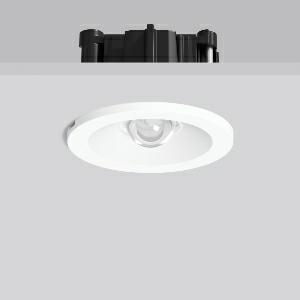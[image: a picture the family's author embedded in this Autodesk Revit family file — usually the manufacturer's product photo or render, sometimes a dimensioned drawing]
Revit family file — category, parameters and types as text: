
# Revit family: turia_l_672413_002_04_6de2
name_source: partatom
category: Lighting Fixtures
units: mm (PartAtom-declared; Revit-internal decimal feet)

## family parameters
Cut with Voids When Loaded = No
Host = Face
Light Source = No
Part Type = Normal
Room Calculation Point = No
Round Connector Dimension = Use Diameter
Shared = No

## types (1)
- TURIA L (1 x LED Modul 765, 270 lm, 6500)
    Apparent Load = 5 VA
    CIE Flux Codes = 16 58 99 100 100
    Color Rendering = 70
    Color Temperature = 6500
    Default Elevation = 1800 mm
    Description = Series: TURIA L
Round emergency luminaire for escape route lighting. Housing: die-cast aluminium. Bezel ring: plastic. With plastic lenses for area lighting. Self-contained system with automatic self-test and feedback to the RZB monitoring system MULTIDIGIT. With enclosed separate ceiling mounting ring also suitable for ceiling cut-outs of Ø 68 mm. 
Colour: white
Diameter: 62 mm
Height: 3 mm
Cut-out diameter: 54-68 mm
Recess height: 76-162 mm
Luminaire: recess height: 42 mm
Weight: 550 g
Operating mode: non-maintained power mode
Duration time: 8 h
Lamp: LED
Socket: without socket
Colour temperature: 6500K
Colour rendering index (CRI): 70
System power: 5.2 W
Rated luminous flux: 270 lm
Luminous flux, emergency: 130 lm
System power, emergency: -
Control gear: Regulated power supply
Protection class: II
Type of protection: IP 20
    Height = 0 mm  [stored 0 ft]
    Lamp = 1 x LED Modul 765
    Lamp Light Flux = 270 lm
    Lamp count = 1
    Length = 62 mm  [stored 0.203412 ft]
    Lifetime = 50000 h
    Luminous efficacy = 52 lm/W
    Manufacturer = RZB
    ModVariant = No
    Model = 672413.002.04
    Mounting Place = Ceiling
    Mounting Type = Recessed
    Number of Poles = 1
    OnlyDefault = Yes
    Power Factor = 1
    Product Name = TURIA L
    Product group = Recessed ceiling luminaires
    ProductGroupID = 405
    Protection Class = Protection class II
    Protection Degree = IP 20
    RLX_Detail_Level = 1
    RLX_Emergency_Light_Flux = 130 lm
    RLX_Emergency_Type = 3
    RLX_Emergency_Type_DB = Yes
    RlxData = <blob elided: 35689 chars, md5=a92c01f5>
    Socket = socket
    Standby Power = 0 W
    System Light Flux = 270 lm
    System Power = 5 W
    Type Comments = Product without accessories
    Type Image = 672412.002.jpg
    URL = http://relux.com
    VarID = ---
    Voltage = 230 V
    Voltage Range = 220-240 V
    Weight = 0.00 kg
    Width = 0 mm  [stored 0 ft]

note: [stored X ft] marks values corroborated as IEEE doubles in the binary element streams (Revit-internal decimal feet)

## geometry (parser evidence)
native form markers: Blend x4, Sweep x9
no freeform markers — native parametric forms only
